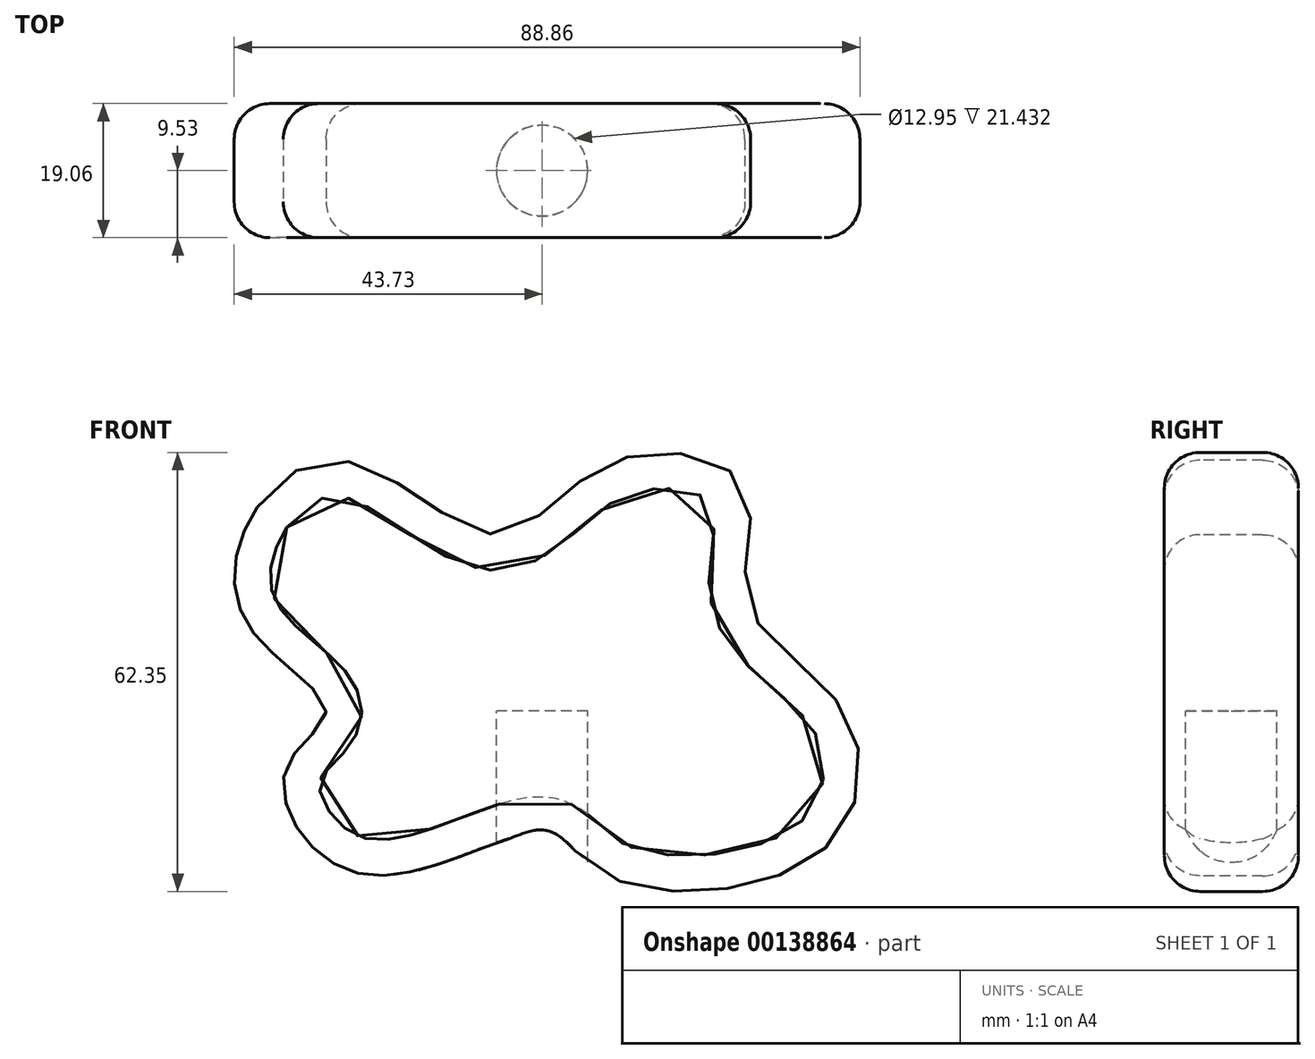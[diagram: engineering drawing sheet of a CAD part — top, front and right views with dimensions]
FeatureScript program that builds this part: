
annotation { "Feature Type Name" : "Feature", "Feature Type Description" : "" }
export const myFeature = defineFeature(function(context is Context, id is Id, definition is map)
    precondition{}
    {
        {
            var Q0;
            Q0=qCreatedBy(makeId("Front.planeOp"),FACE);
            var sketch = newSketch(context, id + "F0", { "sketchPlane" : qUnion([Q0])});
            skFitSpline(sketch, "E0", {"points": [v(-40.42, 28.98) * mm, v(-26.78, 35.3) * mm, v(-6.33, 25.08) * mm, v(9.74, 35.3) * mm, v(28.73, 31.9) * mm, v(29.22, 15.34) * mm, v(42.85, 0) * mm, v(39.93, -19.72) * mm, v(9.74, -23.62) * mm, v(0, -17.29) * mm, v(-25.81, -23.13) * mm, v(-36.52, -8.52) * mm, v(-30.68, 0) * mm, v(-41.88, 12.42) * mm, v(-40.42, 28.98) * mm]});
            skSolve(sketch);
        }
        {
            var Q0;
            Q0=qSketchRegion(id+"F0",true);
            extrude(context, id + "F1", {"entities" : qUnion([Q0]), "endBound" : BoundingType.SYMMETRIC, "depth" : 19.05 * mm});
        }
        {
            var Q0;
            Q0=qCreatedBy(makeId("Top.planeOp"),FACE);
            var sketch = newSketch(context, id + "F2", { "sketchPlane" : qUnion([Q0])});
            skCircle(sketch, "E1", {"center": v(0, 0) * mm, "radius": 6.48 * mm});
            skSolve(sketch);
        }
        {
            var Q0;
            Q0=qSketchRegion(id+"F2",true);
            var Q1;
            Q1=makeQuery(id+"F1.opExtrude","SWEPT_FACE",FACE,{"disambiguationData":[OSD([sQuery(id+"F0.wireOp",EDGE,"E0")])]});
            extrude(context, id + "F3", {"entities" : qUnion([Q0]), "operationType" : NewBodyOperationType.REMOVE, "endBound" : BoundingType.UP_TO_SURFACE, "oppositeDirection" : true, "endBoundEntityFace" : qUnion([Q1]), "depth" : 12.7 * mm});
        }
        {
            var Q0;
            Q0=makeQuery(id+"F1.opExtrude","CAP_EDGE",EDGE,{"disambiguationData":[OSD([sQuery(id+"F0.wireOp",EDGE,"E0")])],"isStart":false});
            var Q1;
            Q1=makeQuery(id+"F1.opExtrude","CAP_EDGE",EDGE,{"disambiguationData":[OSD([sQuery(id+"F0.wireOp",EDGE,"E0")])],"isStart":true});
            fillet(context, id + "F4", {"entities" : qUnion([Q0, Q1]), "radius" : 5.08 * mm, "tangentPropagation" : true, "allowEdgeOverflow" : false});
        }
    });
